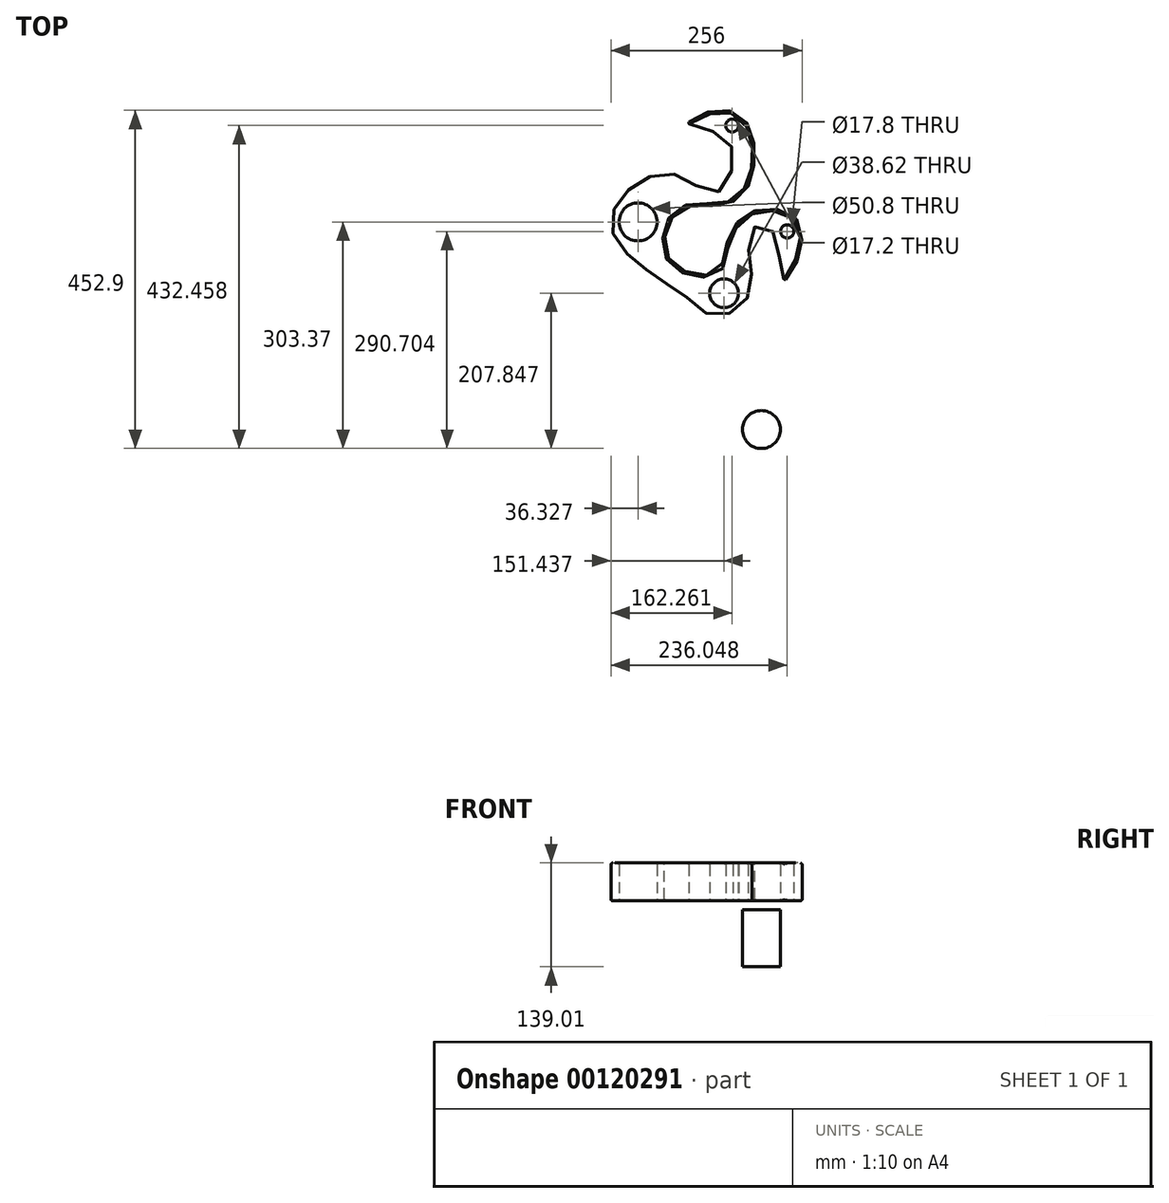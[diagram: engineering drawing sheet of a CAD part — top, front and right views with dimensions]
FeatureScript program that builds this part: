
annotation { "Feature Type Name" : "Feature", "Feature Type Description" : "" }
export const myFeature = defineFeature(function(context is Context, id is Id, definition is map)
    precondition{}
    {
        {
            var Q0;
            Q0=qCreatedBy(makeId("Top.planeOp"),FACE);
            var sketch = newSketch(context, id + "F0", { "sketchPlane" : qUnion([Q0])});
            skFitSpline(sketch, "E0", {"points": [v(-111.49, 38.1) * mm, v(-122.83, -27.51) * mm, v(-61.04, -44.64) * mm, v(-47.16, -9.78) * mm, v(-19.18, 33.22) * mm, v(34.1, 36.25) * mm, v(54.44, 0) * mm, v(31.53, -53.84) * mm, v(19.43, 0) * mm, v(0, 23.32) * mm, v(-16.15, 0) * mm, v(-13.94, -42.5) * mm, v(-19.35, -79.63) * mm, v(-59.9, -103.94) * mm, v(-97.12, -79.79) * mm, v(-201.39, 20.2) * mm, v(-122.14, 88.33) * mm, v(-60.17, 62.36) * mm, v(-44.18, 131.55) * mm, v(-97.02, 155.64) * mm, v(-37.14, 170.52) * mm, v(-11.45, 89.6) * mm, v(-48.13, 46.94) * mm, v(-111.49, 38.1) * mm]});
            skCircle(sketch, "E1", {"center": v(-165.11, 23.25) * mm, "radius": 25.4 * mm});
            skCircle(sketch, "E2", {"center": v(-50, -72.27) * mm, "radius": 19.31 * mm});
            skCircle(sketch, "E3", {"center": v(34.6, 10.58) * mm, "radius": 8.9 * mm});
            skCircle(sketch, "E4", {"center": v(-39.18, 152.34) * mm, "radius": 8.6 * mm});
            skSolve(sketch);
        }
        {
            var Q0;
            Q0=makeQuery(id+"F0.imprint","IMPRINT",FACE,{"disambiguationData":[TD([[makeQuery(id+"F0.imprint","IMPRINT",EDGE,{"derivedFrom":sQuery(id+"F0.wireOp",EDGE,"E0")}),-1.0]])]});
            extrude(context, id + "F1", {"entities" : qUnion([Q0]), "depth" : 50.8 * mm});
        }
        {
            var Q0;
            Q0=makeQuery(id+"F1.opExtrude","SWEPT_FACE",FACE,{"disambiguationData":[OSD([sQuery(id+"F0.wireOp",EDGE,"E1")])]});
            var Q1;
            Q1=makeQuery(id+"F1.opExtrude","SWEPT_FACE",FACE,{"disambiguationData":[OSD([sQuery(id+"F0.wireOp",EDGE,"E2")])]});
            var Q2;
            Q2=makeQuery(id+"F1.opExtrude","SWEPT_FACE",FACE,{"disambiguationData":[OSD([sQuery(id+"F0.wireOp",EDGE,"E3")])]});
            var Q3;
            Q3=makeQuery(id+"F1.opExtrude","SWEPT_FACE",FACE,{"disambiguationData":[OSD([sQuery(id+"F0.wireOp",EDGE,"E4")])]});
            fillet(context, id + "F2", {"entities" : qUnion([Q0, Q1, Q2, Q3]), "radius" : 2.54 * mm, "tangentPropagation" : true, "allowEdgeOverflow" : false});
        }
        {
            var Q0;
            Q0=makeQuery(id+"F1.opExtrude","SWEPT_FACE",FACE,{"disambiguationData":[OSD([sQuery(id+"F0.wireOp",EDGE,"E0")])]});
            fillet(context, id + "F3", {"entities" : qUnion([Q0]), "radius" : 2.54 * mm, "tangentPropagation" : true, "allowEdgeOverflow" : false});
        }
        {
            var Q0;
            Q0=qCreatedBy(makeId("Right.planeOp"),FACE);
            var sketch = newSketch(context, id + "F4", { "sketchPlane" : qUnion([Q0])});
            skLineSegment(sketch, "E5.bottom", {"start": v(-280.12, -12.01) * mm, "end": v(-254.72, -12.01) * mm});
            skLineSegment(sketch, "E5.top", {"start": v(-280.12, -88.21) * mm, "end": v(-254.72, -88.21) * mm});
            skLineSegment(sketch, "E5.left", {"start": v(-280.12, -12.01) * mm, "end": v(-280.12, -88.21) * mm});
            skLineSegment(sketch, "E5.right", {"start": v(-254.72, -12.01) * mm, "end": v(-254.72, -88.21) * mm});
            skSolve(sketch);
        }
        {
            var Q0;
            Q0=makeQuery(id+"F4.imprint","IMPRINT",FACE,{"disambiguationData":[TD([[makeQuery(id+"F4.imprint","IMPRINT",EDGE,{"derivedFrom":sQuery(id+"F4.wireOp",EDGE,"E5.bottom")}),-1.0]])]});
            var Q1;
            Q1=sQuery(id+"F4.wireOp",EDGE,"E5.right");
            revolve(context, id + "F5", {"entities" : qUnion([Q0]), "axis" : qUnion([Q1]), "revolveType" : RevolveType.FULL});
        }
    });
